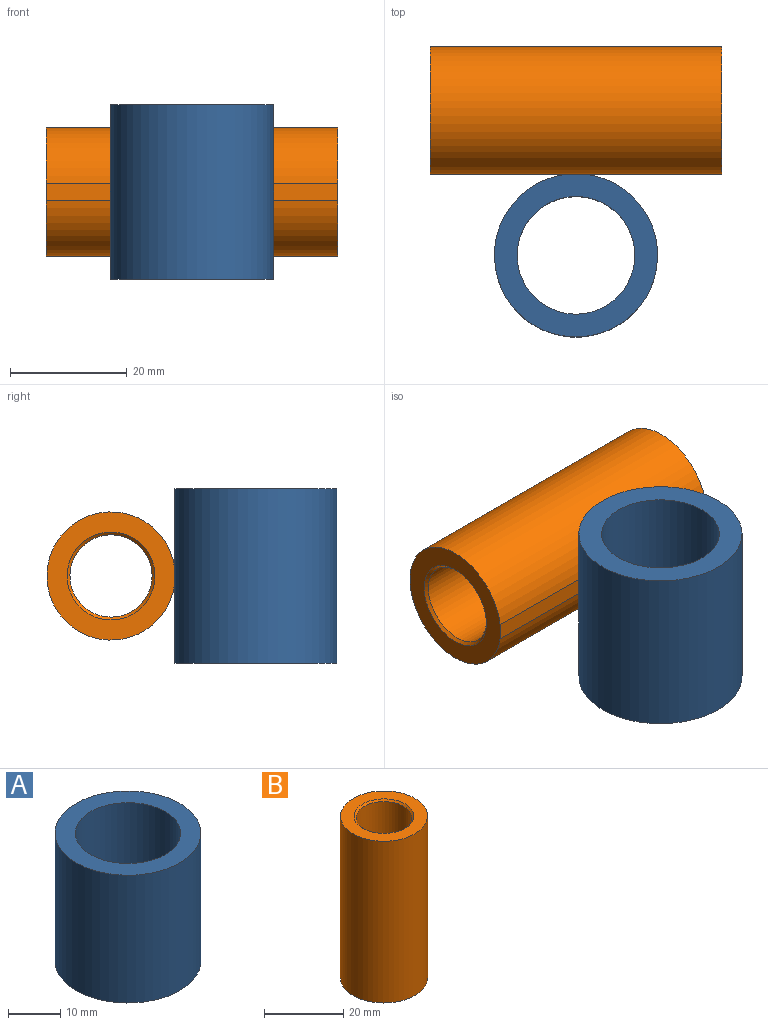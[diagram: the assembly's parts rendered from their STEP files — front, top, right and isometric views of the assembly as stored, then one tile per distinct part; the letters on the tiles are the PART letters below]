
ASSEMBLY  parts=2 mates=1
PART A: 5 faces, bbox 28x27.9x30 mm
  f0: cylinder r=10.1mm len=30mm, axis (0,0,-1), area 1903.8mm2, adj f2,f3
  f1: cylinder r=14mm len=30mm, axis (0,0,-1), area 2538.5mm2, adj f2,f3,f4
  f2: plane 28x27.9mm, normal (0,0,1), area 295.1mm2, adj f0,f1,f4
  f3: plane 28x27.9mm, normal (0,0,-1), area 295.1mm2, adj f0,f1,f4
  f4: plane 30x3.34mm, normal (0,1,0), area 100.2mm2, adj f1,f2,f3
PART B: 7 faces, bbox 22x21.9x50 mm
  f0: cylinder r=7.05mm len=49mm, axis (0,0,-1), area 2170.5mm2, adj f5,f6
  f1: cylinder r=11mm len=50mm, axis (0,0,-1), area 3307.3mm2, adj f2,f3,f4
  f2: plane 22x21.9mm, normal (0,0,1), area 200.9mm2, adj f1,f4,f6
  f3: plane 22x21.9mm, normal (0,0,-1), area 200.9mm2, adj f1,f4,f5
  f4: plane 50x2.96mm, normal (0,1,0), area 148mm2, adj f1,f2,f3
  f5: cone r=7.55mm half-angle=45deg, axis (0,0,-1), area 32.4mm2, adj f0,f3
  f6: cone r=7.05mm half-angle=45deg, axis (0,0,1), area 32.4mm2, adj f0,f2
PLACE A t=(-1.38,14.85,-1.61)mm
PLACE B rot(axis=(0.71,0,-0.71),180deg) t=(23.62,39.65,13.39)mm
MATE fastened B.f4 <-> A.f4  axis (0,-1,0) through (-1.38,28.75,13.39)mm
